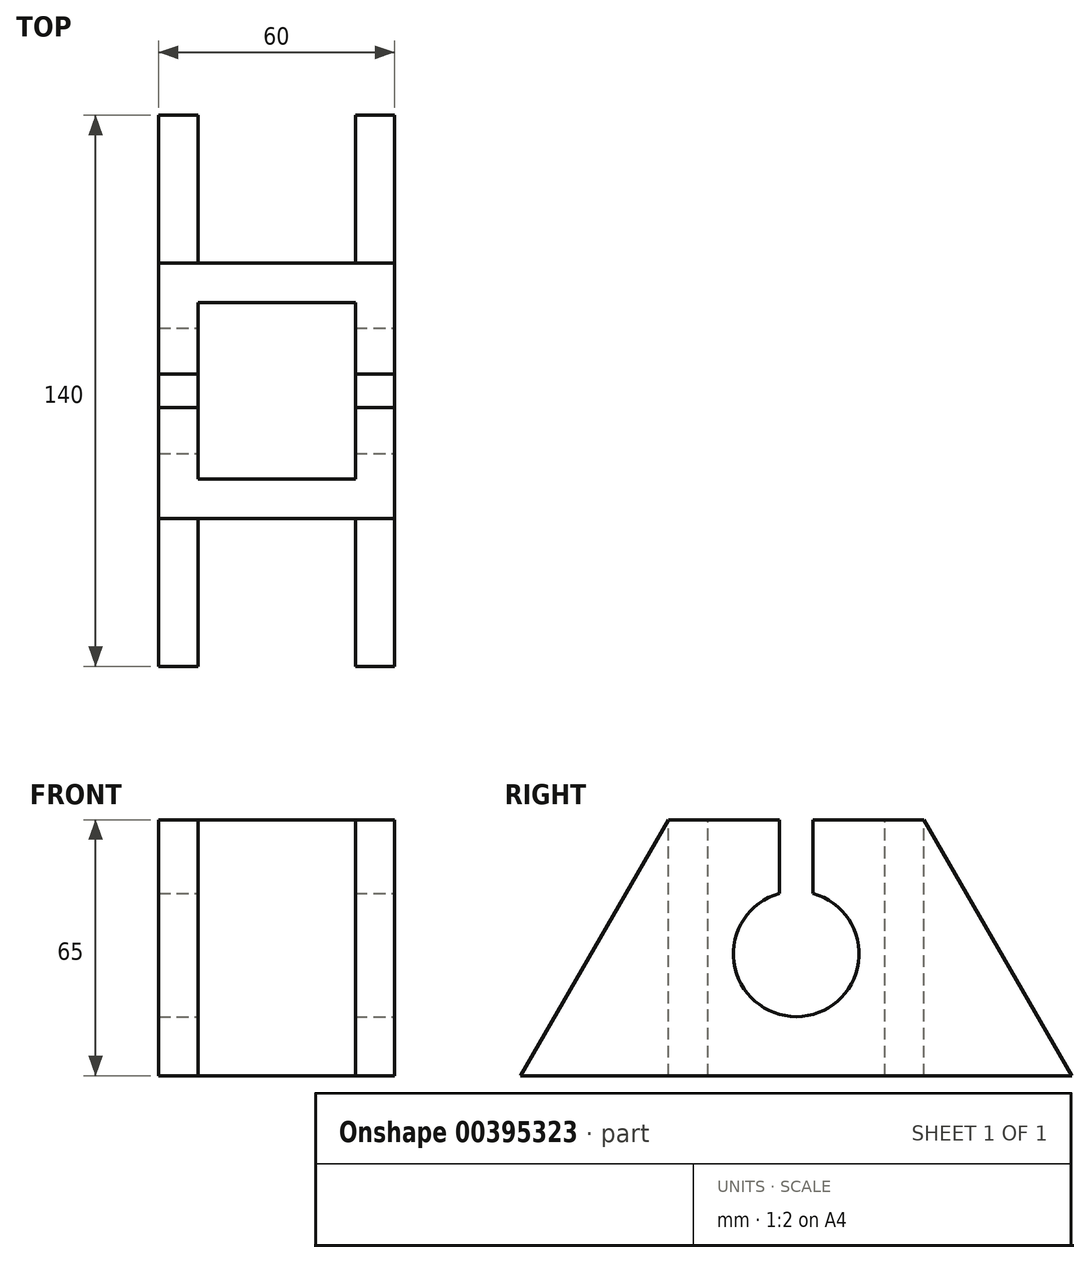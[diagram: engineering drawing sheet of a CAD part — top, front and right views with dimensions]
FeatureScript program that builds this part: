
annotation { "Feature Type Name" : "Feature", "Feature Type Description" : "" }
export const myFeature = defineFeature(function(context is Context, id is Id, definition is map)
    precondition{}
    {
        {
            var Q0;
            Q0=qCreatedBy(makeId("Right.planeOp"),FACE);
            var sketch = newSketch(context, id + "F0", { "sketchPlane" : qUnion([Q0])});
            skLineSegment(sketch, "E0", {"start": v(0, 0) * mm, "end": v(-70, 0) * mm});
            skLineSegment(sketch, "E1", {"start": v(-70, 0) * mm, "end": v(-32.47, 65) * mm});
            skLineSegment(sketch, "E2", {"start": v(-32.47, 65) * mm, "end": v(0, 65) * mm});
            skLineSegment(sketch, "E3.MirrorCS", {"start": v(0, 0) * mm, "end": v(70, 0) * mm});
            skLineSegment(sketch, "E4.MirrorCS", {"start": v(70, 0) * mm, "end": v(32.47, 65) * mm});
            skLineSegment(sketch, "E5.MirrorCS", {"start": v(32.47, 65) * mm, "end": v(0, 65) * mm});
            skSolve(sketch);
        }
        {
            var Q0;
            Q0=makeQuery(id+"F0.imprint","IMPRINT",FACE,{"disambiguationData":[TD([[makeQuery(id+"F0.imprint","IMPRINT",EDGE,{"derivedFrom":sQuery(id+"F0.wireOp",EDGE,"E0")}),-1.0]])]});
            extrude(context, id + "F1", {"entities" : qUnion([Q0]), "depth" : 60 * mm});
        }
        {
            var Q0;
            Q0=makeQuery(id+"F1.opExtrude","SWEPT_FACE",FACE,{"disambiguationData":[OSD([sQuery(id+"F0.wireOp",EDGE,"E2"),sQuery(id+"F0.wireOp",EDGE,"E5.MirrorCS")])]});
            var sketch = newSketch(context, id + "F2", { "sketchPlane" : qUnion([Q0])});
            skLineSegment(sketch, "E6.bottom", {"start": v(10, -32.47) * mm, "end": v(50, -32.47) * mm});
            skLineSegment(sketch, "E6.top", {"start": v(10, -83.98) * mm, "end": v(50, -83.98) * mm});
            skLineSegment(sketch, "E6.left", {"start": v(10, -32.47) * mm, "end": v(10, -83.98) * mm});
            skLineSegment(sketch, "E6.right", {"start": v(50, -32.47) * mm, "end": v(50, -83.98) * mm});
            skLineSegment(sketch, "E7.MirrorCS", {"start": v(10, 32.47) * mm, "end": v(50, 32.47) * mm});
            skLineSegment(sketch, "E8.MirrorCS", {"start": v(10, 83.98) * mm, "end": v(50, 83.98) * mm});
            skLineSegment(sketch, "E9.MirrorCS", {"start": v(50, 32.47) * mm, "end": v(50, 83.98) * mm});
            skLineSegment(sketch, "E10.MirrorCS", {"start": v(10, 32.47) * mm, "end": v(10, 83.98) * mm});
            skSolve(sketch);
        }
        {
            var Q0;
            Q0=makeQuery(id+"F2.imprint","IMPRINT",FACE,{"disambiguationData":[TD([[makeQuery(id+"F2.imprint","IMPRINT",EDGE,{"derivedFrom":sQuery(id+"F2.wireOp",EDGE,"E6.bottom")}),1.0]])]});
            var Q1;
            Q1=makeQuery(id+"F2.imprint","IMPRINT",FACE,{"disambiguationData":[TD([[makeQuery(id+"F2.imprint","IMPRINT",EDGE,{"derivedFrom":sQuery(id+"F2.wireOp",EDGE,"E7.MirrorCS")}),-1.0]])]});
            extrude(context, id + "F3", {"entities" : qUnion([Q0, Q1]), "operationType" : NewBodyOperationType.REMOVE, "oppositeDirection" : true, "depth" : 126 * mm});
        }
        {
            var Q0;
            Q0=makeQuery(id+"F1.opExtrude","SWEPT_FACE",FACE,{"disambiguationData":[OSD([sQuery(id+"F0.wireOp",EDGE,"E2"),sQuery(id+"F0.wireOp",EDGE,"E5.MirrorCS")])]});
            var sketch = newSketch(context, id + "F4", { "sketchPlane" : qUnion([Q0])});
            skLineSegment(sketch, "E11.bottom", {"start": v(10, -22.47) * mm, "end": v(50, -22.47) * mm});
            skLineSegment(sketch, "E11.top", {"start": v(10, 22.47) * mm, "end": v(50, 22.47) * mm});
            skLineSegment(sketch, "E11.left", {"start": v(10, -22.47) * mm, "end": v(10, 22.47) * mm});
            skLineSegment(sketch, "E11.right", {"start": v(50, -22.47) * mm, "end": v(50, 22.47) * mm});
            skPoint(sketch, "E11.middle", {"position": v(30, 0) * mm});
            skSolve(sketch);
        }
        {
            var Q0;
            Q0=makeQuery(id+"F4.imprint","IMPRINT",FACE,{"disambiguationData":[TD([[makeQuery(id+"F4.imprint","IMPRINT",EDGE,{"derivedFrom":sQuery(id+"F4.wireOp",EDGE,"E11.bottom")}),1.0]])]});
            extrude(context, id + "F5", {"entities" : qUnion([Q0]), "operationType" : NewBodyOperationType.REMOVE, "oppositeDirection" : true, "depth" : 92 * mm});
        }
        {
            var Q0;
            Q0=makeQuery(id+"F1.opExtrude","CAP_FACE",FACE,{"disambiguationData":[OSD([sQuery(id+"F0.wireOp",EDGE,"E0"),sQuery(id+"F0.wireOp",EDGE,"E1"),sQuery(id+"F0.wireOp",EDGE,"E2"),sQuery(id+"F0.wireOp",EDGE,"E3.MirrorCS"),sQuery(id+"F0.wireOp",EDGE,"E4.MirrorCS"),sQuery(id+"F0.wireOp",EDGE,"E5.MirrorCS")])],"isStart":false});
            var sketch = newSketch(context, id + "F6", { "sketchPlane" : qUnion([Q0])});
            skArc(sketch, "E12", {"start": v(-4.28, 46.31) * mm, "mid": v(0, 15) * mm, "end": v(4.28, 46.31) * mm});
            skLineSegment(sketch, "E13", {"start": v(-4.28, 46.31) * mm, "end": v(-4.28, 65) * mm});
            skLineSegment(sketch, "E14", {"start": v(-4.28, 65) * mm, "end": v(4.28, 65) * mm});
            skLineSegment(sketch, "E15", {"start": v(4.28, 65) * mm, "end": v(4.28, 46.31) * mm});
            skSolve(sketch);
        }
        {
            var Q0;
            Q0=makeQuery(id+"F6.imprint","IMPRINT",FACE,{"disambiguationData":[TD([[makeQuery(id+"F6.imprint","IMPRINT",EDGE,{"derivedFrom":sQuery(id+"F6.wireOp",EDGE,"E12")}),1.0]])]});
            extrude(context, id + "F7", {"entities" : qUnion([Q0]), "operationType" : NewBodyOperationType.REMOVE, "oppositeDirection" : true, "depth" : 76 * mm});
        }
    });
